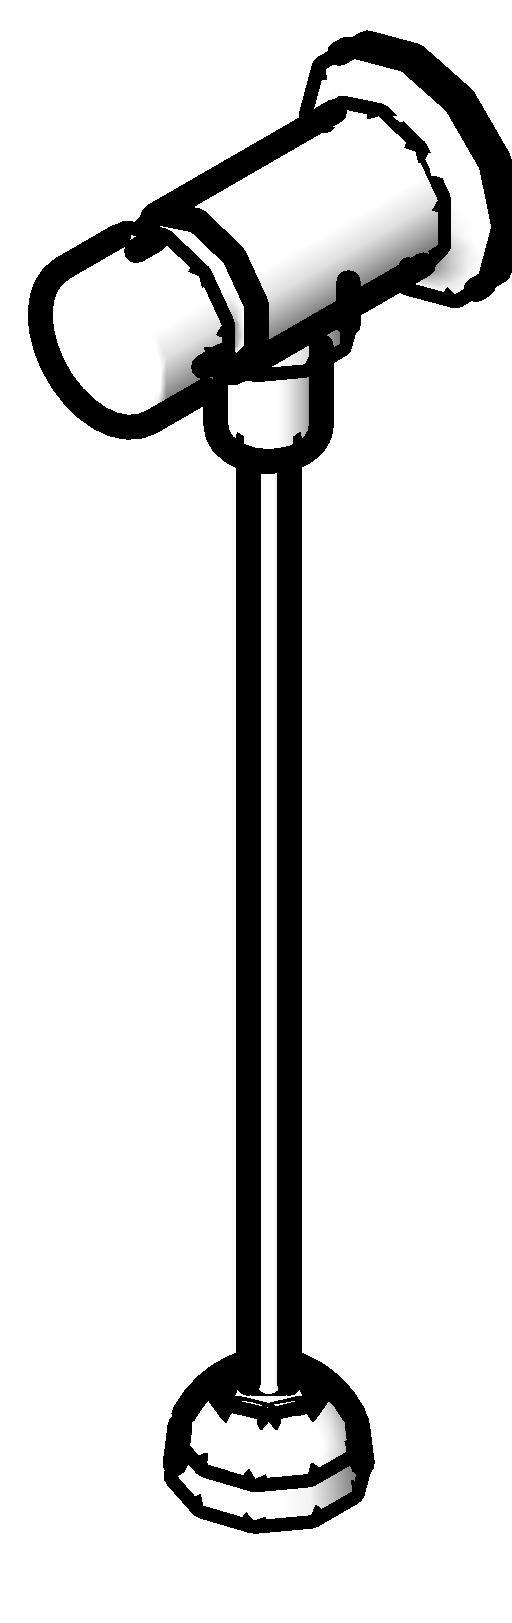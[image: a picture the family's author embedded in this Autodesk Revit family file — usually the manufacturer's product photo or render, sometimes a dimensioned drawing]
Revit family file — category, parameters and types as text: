
# Revit family: Deca_Valvula para mictorio fechamento automatico_Decamatic_2570
name_source: partatom
category: Plumbing Fixtures
units: mm (PartAtom-declared; Revit-internal decimal feet)

## family parameters
Cut with Voids When Loaded = No
Host = Face
Part Type = Normal
Room Calculation Point = No
Round Connector Dimension = Use Radius
Shared = No

## types (1)
- 2570.C_Cromado_DN15
    Acompanha o Produto = Acompanha Flexivel
    Aprovado por = quattroD
    Atendimento ao Cliente = 0800-0117073
    CWFU = 0
    Categoria = SISTEMAS DE DESCARGA
    Composição Anel Vedação = -
    Composição Assento = -
    Composição Básica = Liga de Cobre (bronze e latão),Plásticos de Engenharia,Elastômeros
    Composição Componente = -
    Consumo = Váriavel
    Cor Interna = -
    Cor Principal = Cromado
    Cor Secundária = -
    Cores Componente = -
    Criado por = quattroD
    Código Pai = 2570
    Default Elevation = 1100 mm
    Description = Válvula de mictório com fechamento automático
    Diâmetro Água Fria = 15 mm  [stored 0.0492126 ft]
    Diâmetro Água Fria Saída = 15 mm  [stored 0.0492126 ft]
    HWFU = 0
    Informações Complementares = -
    Itens de Instalação = -
    Linha = Decamatic
    Manufacturer = Deca
    Material = Deca_Cromado
    Model = 2570.C
    Norma = NBR13713
    Peso Líquido (Kg) = 1.071
    Pressão máx. funcionamento = 40 MCA
    Pressão mín. Aquec. Acúmulo = -
    Pressão mín. Aquec. Passagem = -
    Pressão mín. funcionamento = 2 MCA
    Raio Água Fria = 8 mm  [stored 0.0262467 ft]
    Raio Água Fria Saída = 8 mm  [stored 0.0262467 ft]
    Saída de Esgoto = -
    Segmento = Banheiro Médio
    Tipo de dispositivo economizador = Sim
    Tipo de mecanismo utilizado = -
    Tipo de rosca de entrada = BSP NBR 8133
    Tipo de rosca de saída = BSP NBR 8133
    URL = www.deca.com.br
    Vazão na Pressão máx. (L/min) = 18
    Vazão na Pressão mín. (L/min) = 4

note: source unit labels omitted for Vazão na Pressão máx. (L/min), Vazão na Pressão mín. (L/min) — the stored unit's dimension contradicts the parameter name (converter mislabeling)

note: [stored X ft] marks values corroborated as IEEE doubles in the binary element streams (Revit-internal decimal feet)

## geometry (parser evidence)
native form markers: Sweep x2
no freeform markers — native parametric forms only
